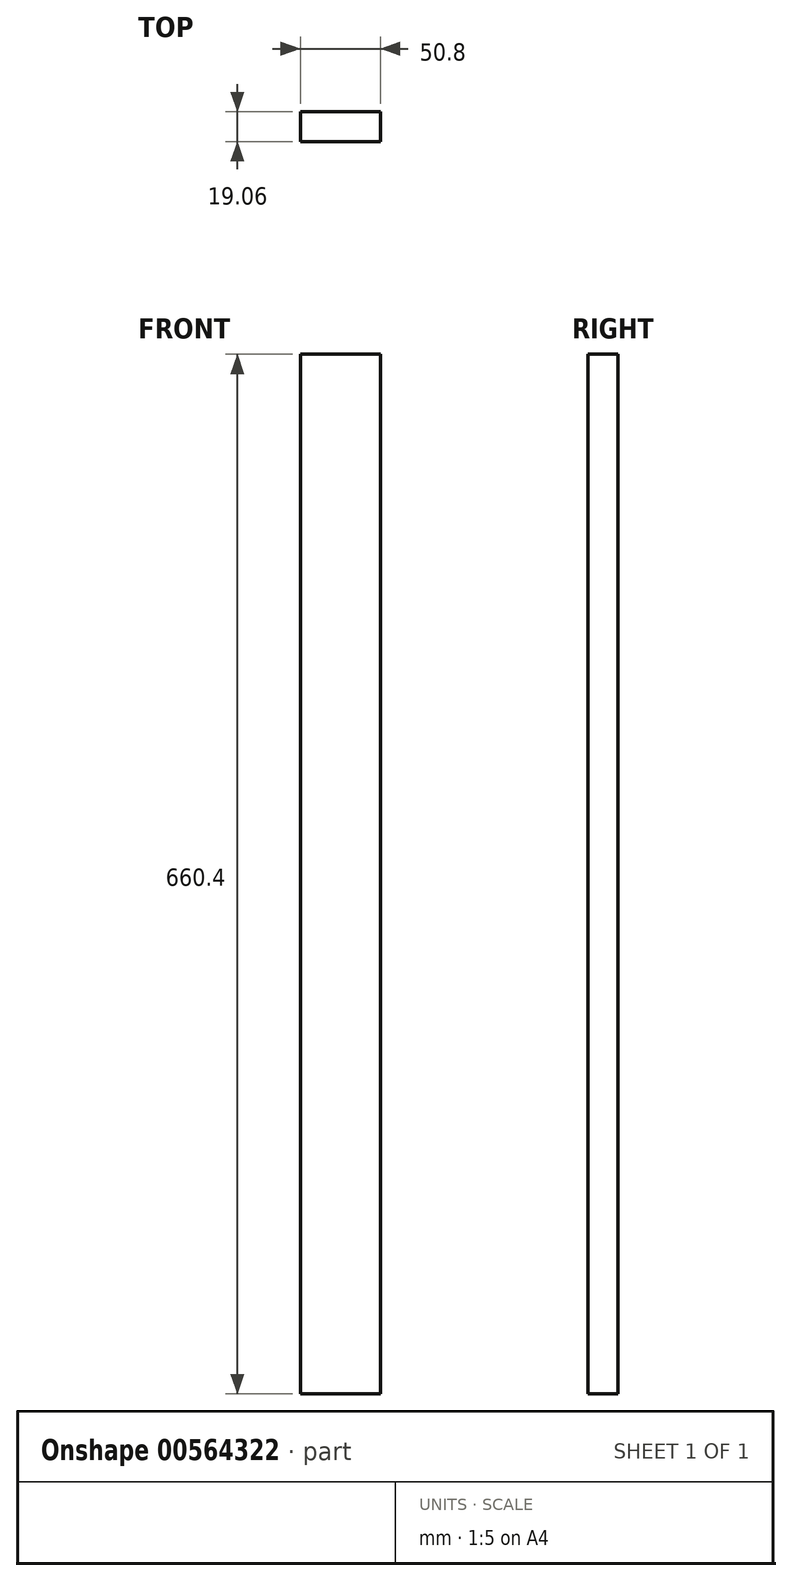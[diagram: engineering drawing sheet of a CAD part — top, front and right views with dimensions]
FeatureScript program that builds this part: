
annotation { "Feature Type Name" : "Feature", "Feature Type Description" : "" }
export const myFeature = defineFeature(function(context is Context, id is Id, definition is map)
    precondition{}
    {
        {
            var Q0;
            Q0=qCreatedBy(makeId("Top.planeOp"),FACE);
            var sketch = newSketch(context, id + "F0", { "sketchPlane" : qUnion([Q0])});
            skLineSegment(sketch, "E0.bottom", {"start": v(-25.4, 9.53) * mm, "end": v(25.4, 9.53) * mm});
            skLineSegment(sketch, "E0.top", {"start": v(-25.4, -9.53) * mm, "end": v(25.4, -9.53) * mm});
            skLineSegment(sketch, "E0.left", {"start": v(-25.4, 9.53) * mm, "end": v(-25.4, -9.53) * mm});
            skLineSegment(sketch, "E0.right", {"start": v(25.4, 9.53) * mm, "end": v(25.4, -9.53) * mm});
            skPoint(sketch, "E0.middle", {"position": v(0, 0) * mm});
            skSolve(sketch);
        }
        {
            var Q0;
            Q0 = qSketchRegion(id + "F0", true);
            extrude(context, id + "F1", {"entities" : qUnion([Q0]), "depth" : 660.4 * mm, "offsetDistance" : 25.4 * mm});
        }
    });
